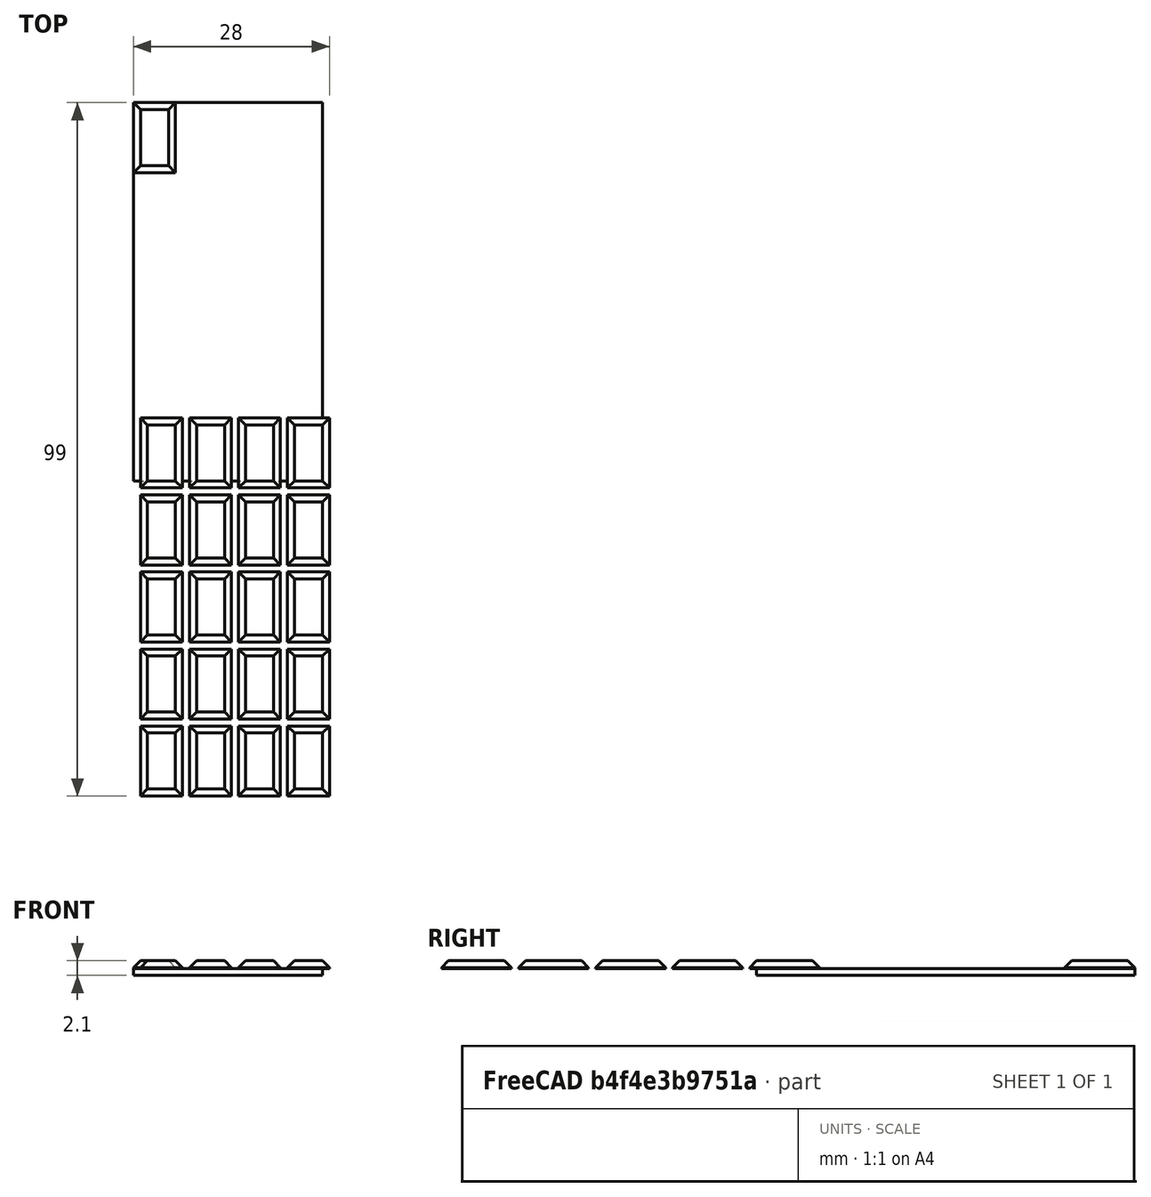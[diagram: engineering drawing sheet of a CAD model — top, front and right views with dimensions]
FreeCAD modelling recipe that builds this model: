
FCSTD DOCUMENT  (FreeCAD 0.20R29603 (Git))
Label: OJT1_T04R10_chocolata
License: All rights reserved
LicenseURL: http://en.wikipedia.org/wiki/All_rights_reserved
objects: Part::Box×2, Part::Chamfer×1, Part::FeaturePython×1, Part::MultiFuse×1
note: 5 computed .brp shape members not serialized (recipe doc carries the construction recipe); baked Part::Feature solids carry a one-line shape summary decoded from their .brp

FEATURE [Part::Box] Box  label="Cub"
  AttacherType = Attacher::AttachEngine3D
  Height = 1.1
  Length = 6
  Width = 10
FEATURE [Part::Chamfer] Chamfer  label="Xamfrà"
  Base = -> Box
  Edges = 4 edges r=1: [Edge2,Edge6,Edge10,Edge12]
FEATURE [Part::FeaturePython] Array  # Draft array (typed FeaturePython)
  Angle = 360
  ArrayType = 0
  Axis = (0,0,1)
  Base = -> Chamfer
  Center = (0,0,0)
  IntervalX = (7,0,0)
  IntervalY = (0,-11,0)
  IntervalZ = (0,0,1)
  NumberPolar = 1
  NumberX = 4
  NumberY = 5
  NumberZ = 1
FEATURE [Part::Box] Box001  label="Cub001"
  AttacherType = Attacher::AttachEngine3D
  Height = 1
  Length = 27
  Placement = pos=(0,-44,-1) rot=(0,0,1;0rad)
  Width = 54
FEATURE [Part::MultiFuse] Fusion  label="Unió"
  Placement = pos=(-1,45,0) rot=(0,0,1;0rad)
  Shapes = -> [Chamfer,Box001]
